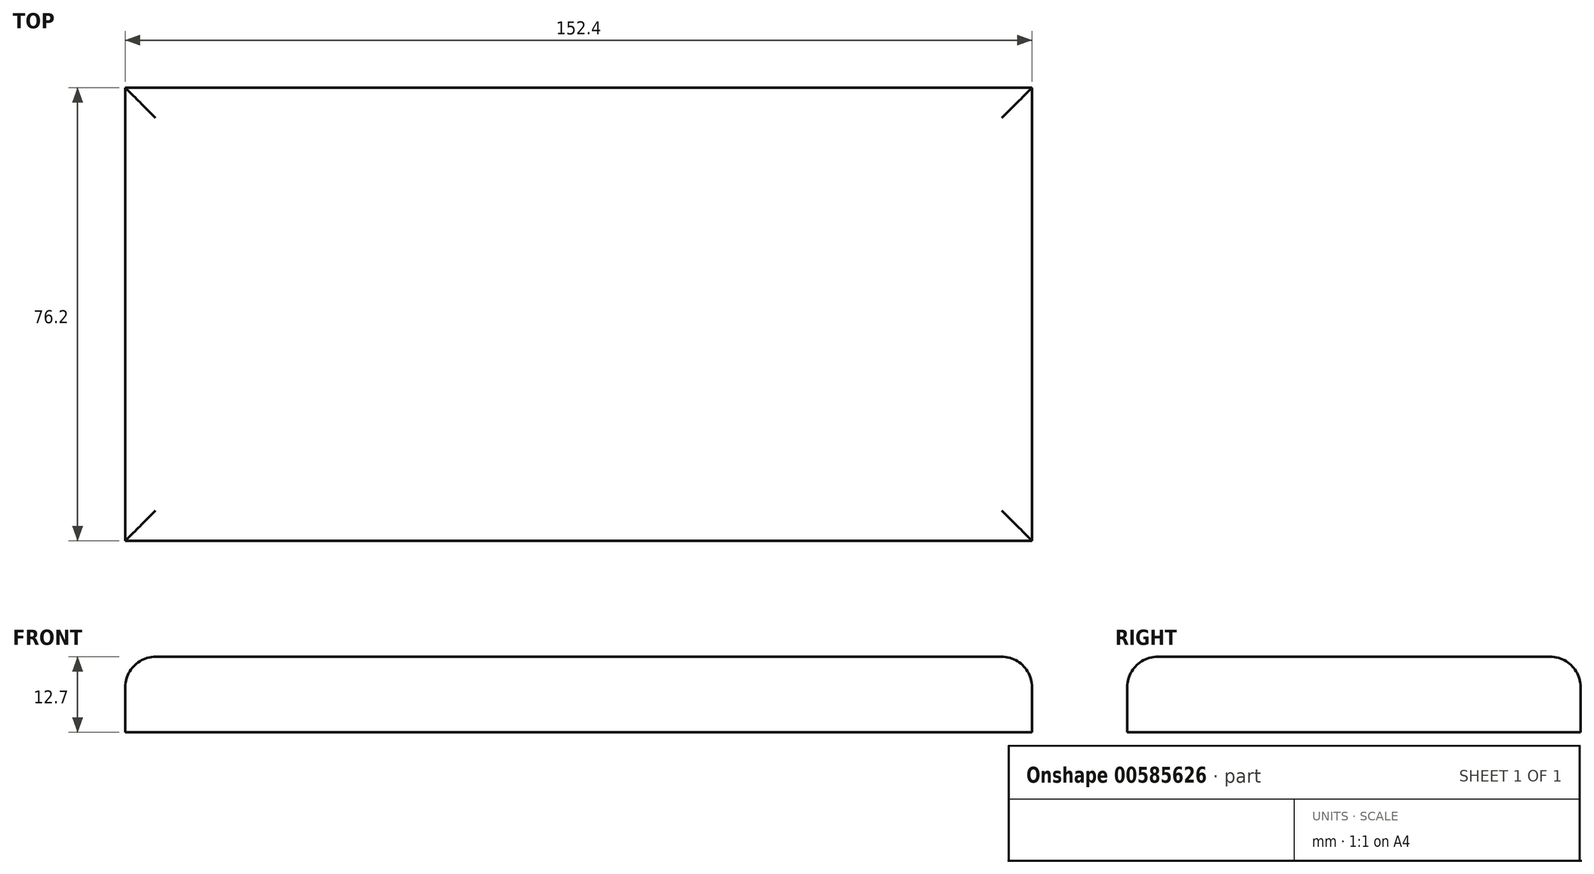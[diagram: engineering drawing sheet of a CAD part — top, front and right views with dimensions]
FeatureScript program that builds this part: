
annotation { "Feature Type Name" : "Feature", "Feature Type Description" : "" }
export const myFeature = defineFeature(function(context is Context, id is Id, definition is map)
    precondition{}
    {
        {
            var Q0;
            Q0=qCreatedBy(makeId("Top.planeOp"),FACE);
            var sketch = newSketch(context, id + "F0", { "sketchPlane" : qUnion([Q0])});
            skLineSegment(sketch, "E0.bottom", {"start": v(-76.2, 38.1) * mm, "end": v(76.2, 38.1) * mm});
            skLineSegment(sketch, "E0.top", {"start": v(-76.2, -38.1) * mm, "end": v(76.2, -38.1) * mm});
            skLineSegment(sketch, "E0.left", {"start": v(-76.2, 38.1) * mm, "end": v(-76.2, -38.1) * mm});
            skLineSegment(sketch, "E0.right", {"start": v(76.2, 38.1) * mm, "end": v(76.2, -38.1) * mm});
            skPoint(sketch, "E0.middle", {"position": v(0, 0) * mm});
            skSolve(sketch);
        }
        {
            var Q0;
            Q0=qSketchRegion(id+"F0",true);
            extrude(context, id + "F1", {"entities" : qUnion([Q0]), "depth" : 12.7 * mm});
        }
        {
            var Q0;
            Q0=makeQuery(id+"F1.opExtrude","CAP_EDGE",EDGE,{"disambiguationData":[OSD([sQuery(id+"F0.wireOp",EDGE,"E0.right")])],"isStart":false});
            var Q1;
            Q1=makeQuery(id+"F1.opExtrude","CAP_EDGE",EDGE,{"disambiguationData":[OSD([sQuery(id+"F0.wireOp",EDGE,"E0.left")])],"isStart":false});
            var Q2;
            Q2=makeQuery(id+"F1.opExtrude","CAP_EDGE",EDGE,{"disambiguationData":[OSD([sQuery(id+"F0.wireOp",EDGE,"E0.top")])],"isStart":false});
            var Q3;
            Q3=makeQuery(id+"F1.opExtrude","CAP_EDGE",EDGE,{"disambiguationData":[OSD([sQuery(id+"F0.wireOp",EDGE,"E0.bottom")])],"isStart":false});
            fillet(context, id + "F2", {"entities" : qUnion([Q0, Q1, Q2, Q3]), "radius" : 5.08 * mm, "tangentPropagation" : true, "allowEdgeOverflow" : false});
        }
    });
